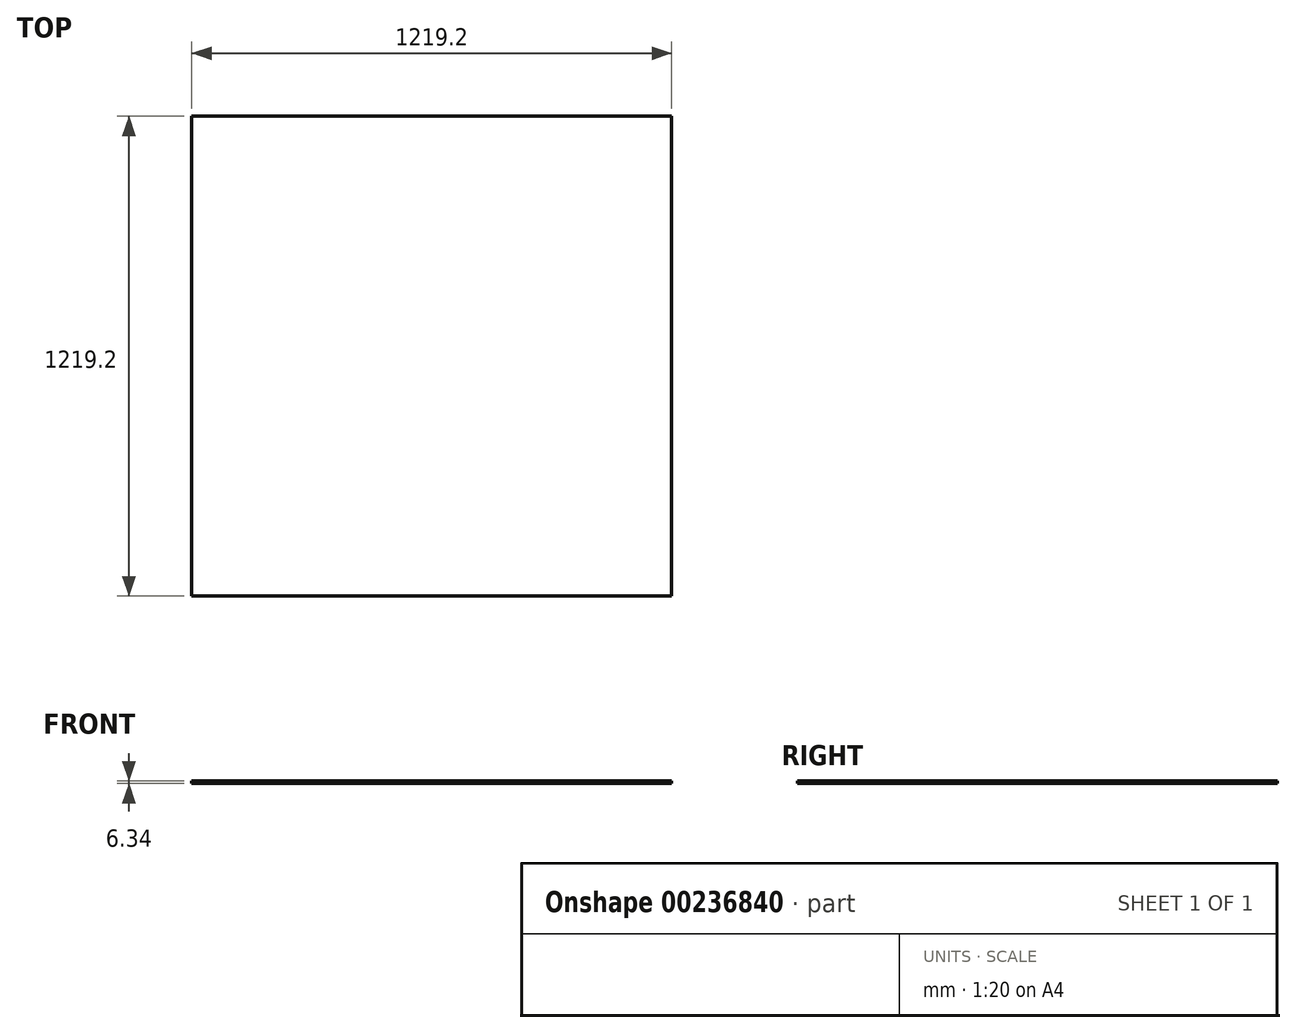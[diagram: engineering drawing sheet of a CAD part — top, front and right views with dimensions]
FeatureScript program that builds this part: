
annotation { "Feature Type Name" : "Feature", "Feature Type Description" : "" }
export const myFeature = defineFeature(function(context is Context, id is Id, definition is map)
    precondition{}
    {
        {
            var Q0;
            Q0=qCreatedBy(makeId("Top.planeOp"),FACE);
            var sketch = newSketch(context, id + "F0", { "sketchPlane" : qUnion([Q0])});
            skLineSegment(sketch, "E0.bottom", {"start": v(609.6, 609.6) * mm, "end": v(-609.6, 609.6) * mm});
            skLineSegment(sketch, "E0.top", {"start": v(609.6, -609.6) * mm, "end": v(-609.6, -609.6) * mm});
            skLineSegment(sketch, "E0.left", {"start": v(609.6, 609.6) * mm, "end": v(609.6, -609.6) * mm});
            skLineSegment(sketch, "E0.right", {"start": v(-609.6, 609.6) * mm, "end": v(-609.6, -609.6) * mm});
            skPoint(sketch, "E0.middle", {"position": v(0, 0) * mm});
            skSolve(sketch);
        }
        {
            var Q0;
            Q0=qSketchRegion(id+"F0",true);
            extrude(context, id + "F1", {"entities" : qUnion([Q0]), "endBound" : BoundingType.SYMMETRIC, "depth" : 6.35 * mm});
        }
    });
